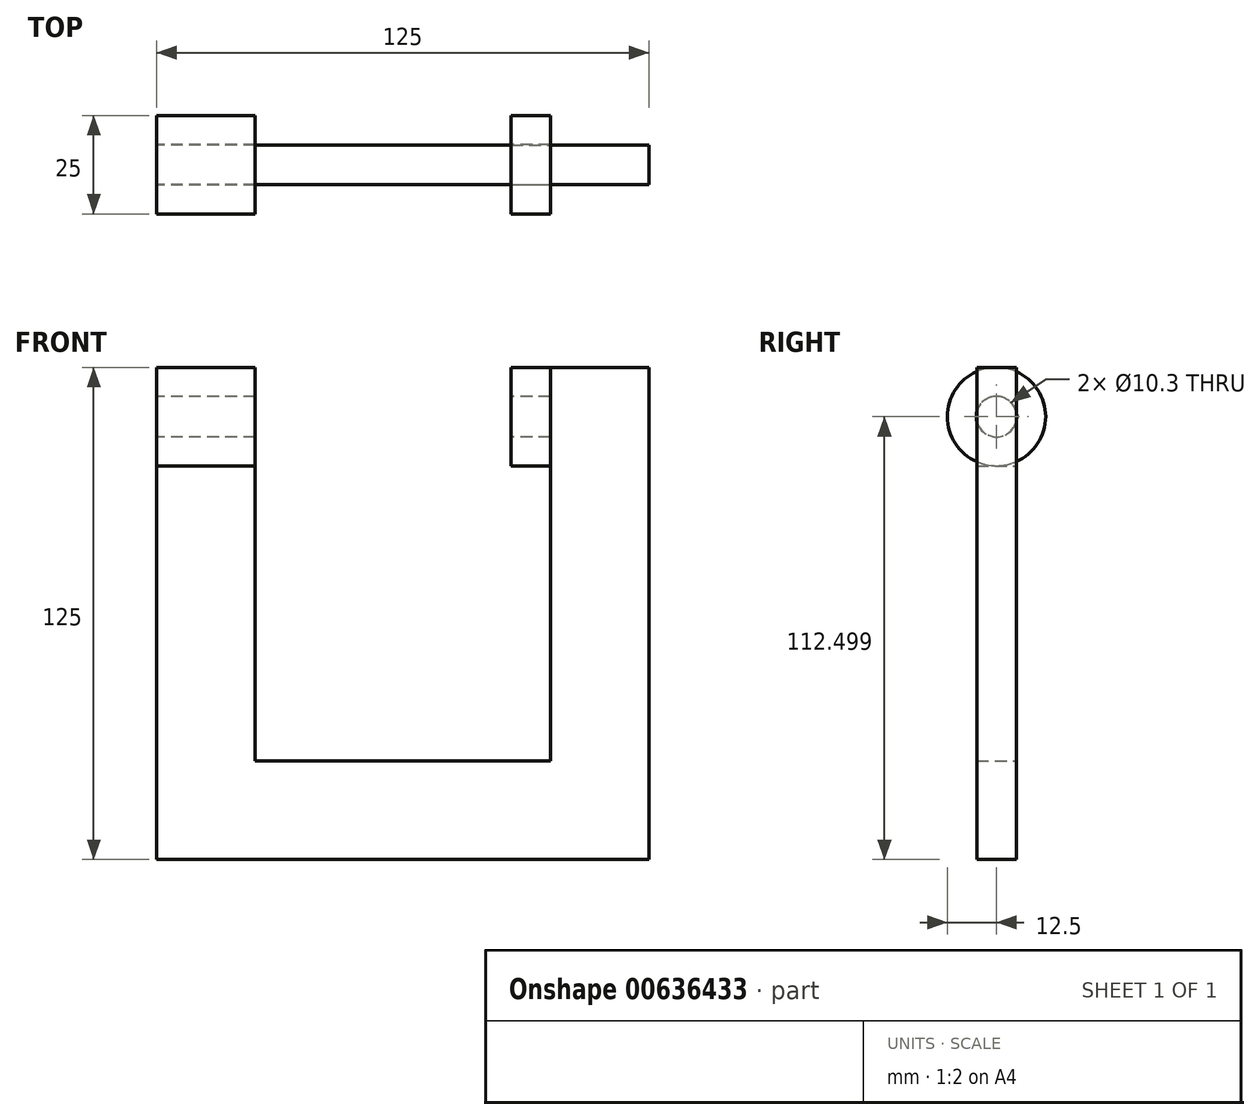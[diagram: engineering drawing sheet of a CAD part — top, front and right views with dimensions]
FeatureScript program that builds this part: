
annotation { "Feature Type Name" : "Feature", "Feature Type Description" : "" }
export const myFeature = defineFeature(function(context is Context, id is Id, definition is map)
    precondition{}
    {
        {
            var Q0;
            Q0=qCreatedBy(makeId("Front.planeOp"),FACE);
            var sketch = newSketch(context, id + "F0", { "sketchPlane" : qUnion([Q0])});
            skLineSegment(sketch, "E0.bottom", {"start": v(-71.17, 53.95) * mm, "end": v(53.83, 53.95) * mm});
            skLineSegment(sketch, "E0.top", {"start": v(-71.17, -71.05) * mm, "end": v(53.83, -71.05) * mm});
            skLineSegment(sketch, "E0.left", {"start": v(-71.17, 53.95) * mm, "end": v(-71.17, -71.05) * mm});
            skLineSegment(sketch, "E0.right", {"start": v(53.83, 53.95) * mm, "end": v(53.83, -71.05) * mm});
            skLineSegment(sketch, "E1", {"start": v(-46.17, 53.95) * mm, "end": v(-46.17, 28.95) * mm});
            skLineSegment(sketch, "E2", {"start": v(-46.17, 28.95) * mm, "end": v(-71.17, 28.95) * mm});
            skLineSegment(sketch, "E3", {"start": v(-46.17, 28.95) * mm, "end": v(-46.17, -46.05) * mm});
            skLineSegment(sketch, "E4", {"start": v(28.83, 53.95) * mm, "end": v(28.83, -46.05) * mm});
            skLineSegment(sketch, "E5", {"start": v(-46.17, -46.05) * mm, "end": v(28.83, -46.05) * mm});
            skSolve(sketch);
        }
        {
            var Q0;
            {var subQ2=sQuery(id+"F0.wireOp",EDGE,"E0.top");Q0=makeQuery(id+"F0.imprint","IMPRINT",FACE,{"disambiguationData":[TD([[makeQuery(id+"F0.imprint","IMPRINT",EDGE,{"derivedFrom":subQ2}),1.0]])]});}
            extrude(context, id + "F1", {"entities" : qUnion([Q0]), "endBound" : BoundingType.SYMMETRIC, "depth" : 10 * mm, "offsetDistance" : 25 * mm});
        }
        {
            var Q0;
            Q0=makeQuery(id+"F1.opExtrude","SWEPT_FACE",FACE,{"disambiguationData":[OSD([sQuery(id+"F0.wireOp",EDGE,"E4")])]});
            var sketch = newSketch(context, id + "F2", { "sketchPlane" : qUnion([Q0])});
            skCircle(sketch, "E6", {"center": v(0, 41.45) * mm, "radius": 12.5 * mm});
            skSolve(sketch);
        }
        {
            var Q0;
            Q0 = qSketchRegion(id + "F2", true);
            extrude(context, id + "F3", {"entities" : qUnion([Q0]), "depth" : 100 * mm, "offsetDistance" : 25 * mm});
        }
        {
            var Q0;
            Q0=qCreatedBy(makeId("Front.planeOp"),FACE);
            var sketch = newSketch(context, id + "F4", { "sketchPlane" : qUnion([Q0])});
            skLineSegment(sketch, "E7", {"start": v(-46.17, 29.4) * mm, "end": v(-46.17, 54.4) * mm});
            skLineSegment(sketch, "E8", {"start": v(18.83, 53.83) * mm, "end": v(18.83, 28.42) * mm});
            skLineSegment(sketch, "E9.bottom", {"start": v(-46.17, 54.4) * mm, "end": v(18.83, 54.4) * mm});
            skLineSegment(sketch, "E9.top", {"start": v(-46.17, 28.42) * mm, "end": v(18.83, 28.42) * mm});
            skLineSegment(sketch, "E9.left", {"start": v(-46.17, 54.4) * mm, "end": v(-46.17, 28.42) * mm});
            skLineSegment(sketch, "E9.right", {"start": v(18.83, 54.4) * mm, "end": v(18.83, 28.42) * mm});
            skSolve(sketch);
        }
        {
            var Q0;
            Q0 = qSketchRegion(id + "F4", true);
            extrude(context, id + "F5", {"entities" : qUnion([Q0]), "operationType" : NewBodyOperationType.REMOVE, "endBound" : BoundingType.SYMMETRIC, "oppositeDirection" : true, "depth" : 25 * mm, "offsetDistance" : 25 * mm});
        }
        {
            var Q0;
            Q0=makeQuery(id+"F3.opExtrude","CAP_FACE",FACE,{"disambiguationData":[OSD([sQuery(id+"F2.wireOp",EDGE,"E6")])],"isStart":false});
            var sketch = newSketch(context, id + "F6", { "sketchPlane" : qUnion([Q0])});
            skLineSegment(sketch, "E10", {"start": v(0, 11.15) * mm, "end": v(0, 41.45) * mm, "construction": true});
            skSolve(sketch);
        }
        {
            var Q0;
            Q0=sQuery(id+"F6.wireOp",VERTEX,"E10.end");
            var Q1;
            Q1=makeQuery(id+"F5.boolean.opBoolean","SPLIT",BODY,{"disambiguationData":[OD(1.0)],"derivedFrom":makeQuery(id+"F3.opExtrude","SWEPT_BODY",BODY,{"disambiguationData":[OSD([sQuery(id+"F2.wireOp",EDGE,"E6")])]})});
            hole(context, id + "F7", {"style" : HoleStyle.SIMPLE, "endStyle" : HoleEndStyle.THROUGH, "standardTappedOrClearance" : lookupTablePath({ "standard" : "ISO", "engagement" : "75%", "pitch" : "1.75 mm", "size" : "M12", "type" : "Tapped" }), "standardBlindInLast" : lookupTablePath({ "standard" : "ISO", "engagement" : "75%", "pitch" : "1.75 mm", "size" : "M12", "type" : "Tapped" }), "holeDiameter" : 10.3 * mm, "majorDiameter" : 12 * mm, "showTappedDepth" : true, "isTappedThrough" : true, "tappedDepth" : 12 * mm, "tapClearance" : 3, "locations" : qUnion([Q0]), "scope" : qUnion([Q1])});
        }
    });
